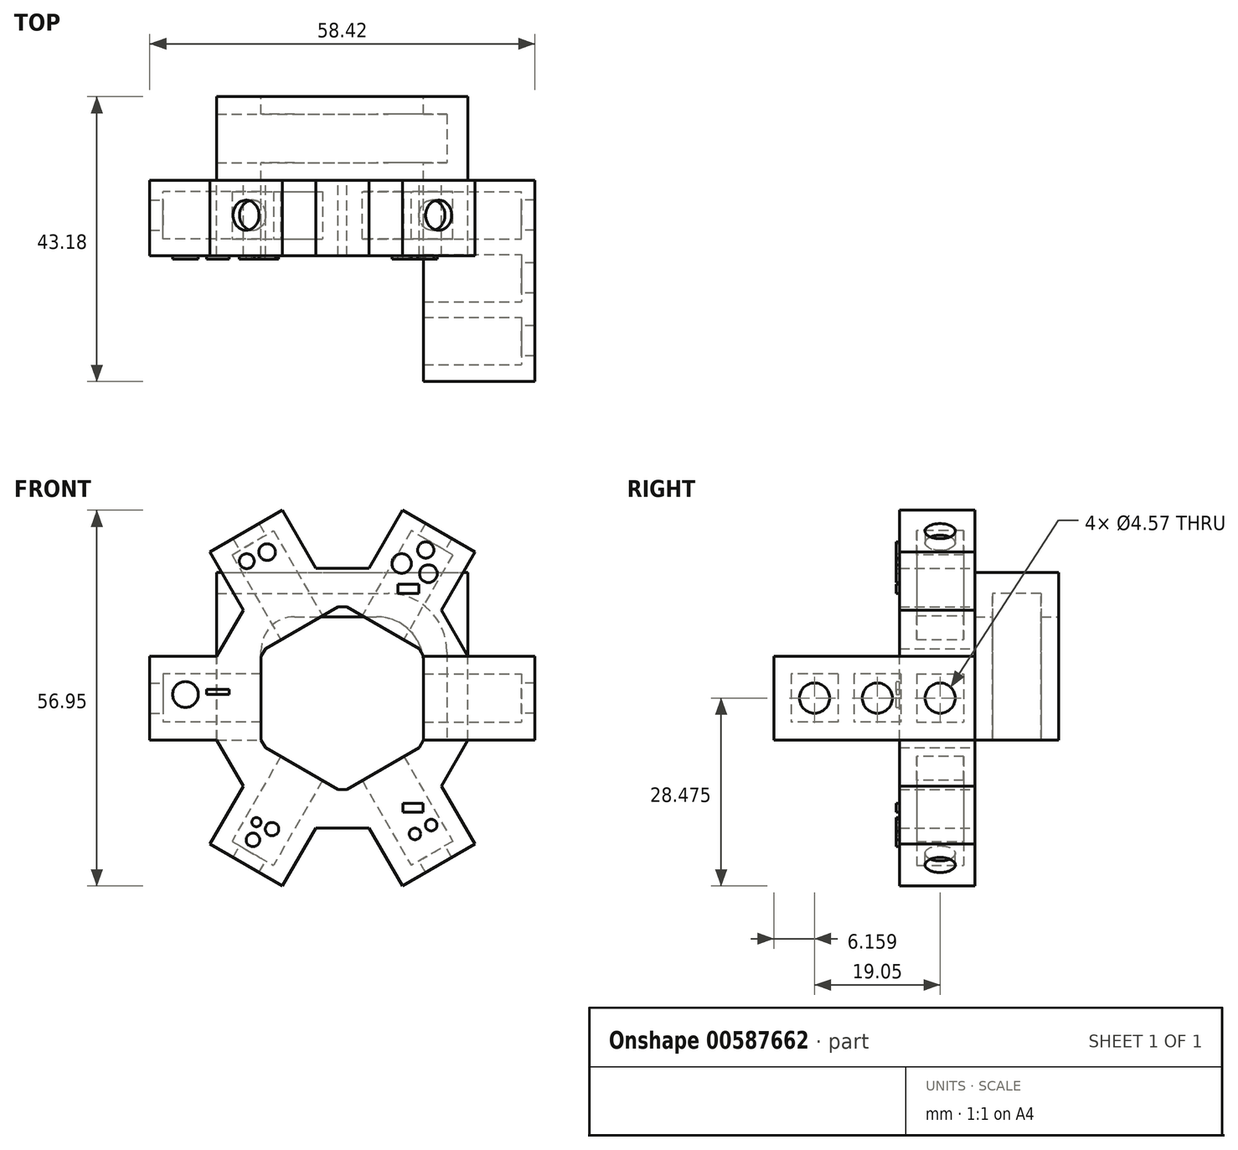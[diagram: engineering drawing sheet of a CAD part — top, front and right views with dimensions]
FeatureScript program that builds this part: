
annotation { "Feature Type Name" : "Feature", "Feature Type Description" : "" }
export const myFeature = defineFeature(function(context is Context, id is Id, definition is map)
    precondition{}
    {
        {
            var Q0;
            Q0=qCreatedBy(makeId("Front.planeOp"),FACE);
            var sketch = newSketch(context, id + "F0", { "sketchPlane" : qUnion([Q0])});
            skLineSegment(sketch, "E0", {"start": v(0, 0) * mm, "end": v(13.34, 0) * mm});
            skLineSegment(sketch, "E1", {"start": v(22.23, -8.89) * mm, "end": v(22.23, -22.23) * mm});
            skPoint(sketch, "E2.visualSharp", {"position": v(22.23, 0) * mm});
            skArc(sketch, "E2.filletArc", {"start": v(22.23, -8.89) * mm, "mid": v(19.62, -2.6) * mm, "end": v(13.34, 0) * mm});
            skLineSegment(sketch, "E3", {"start": v(0, 0) * mm, "end": v(0, 3.18) * mm});
            skLineSegment(sketch, "E4", {"start": v(0, 3.18) * mm, "end": v(25.4, 3.18) * mm});
            skLineSegment(sketch, "E5", {"start": v(25.4, 3.18) * mm, "end": v(25.4, -22.23) * mm});
            skLineSegment(sketch, "E6", {"start": v(25.4, -22.23) * mm, "end": v(22.23, -22.23) * mm});
            skLineSegment(sketch, "E7", {"start": v(0, -3.56) * mm, "end": v(0, 0) * mm});
            skLineSegment(sketch, "E8", {"start": v(18.67, -22.23) * mm, "end": v(22.23, -22.23) * mm});
            skLineSegment(sketch, "E9", {"start": v(0, -3.56) * mm, "end": v(11.56, -3.56) * mm});
            skLineSegment(sketch, "E10", {"start": v(18.67, -10.67) * mm, "end": v(18.67, -22.23) * mm});
            skPoint(sketch, "E11.visualSharp", {"position": v(18.67, -3.56) * mm});
            skArc(sketch, "E11.filletArc", {"start": v(18.67, -10.67) * mm, "mid": v(16.59, -5.64) * mm, "end": v(11.56, -3.56) * mm});
            skLineSegment(sketch, "E12", {"start": v(0, 3.18) * mm, "end": v(-12.7, 3.18) * mm});
            skLineSegment(sketch, "E13", {"start": v(-12.7, 3.17) * mm, "end": v(-12.7, -22.23) * mm});
            skLineSegment(sketch, "E14", {"start": v(0, 0) * mm, "end": v(-12.7, 0) * mm});
            skLineSegment(sketch, "E15", {"start": v(0, -3.56) * mm, "end": v(-0.89, -3.56) * mm});
            skLineSegment(sketch, "E16", {"start": v(-12.7, -22.23) * mm, "end": v(-5.97, -22.23) * mm});
            skLineSegment(sketch, "E17", {"start": v(-5.97, -22.23) * mm, "end": v(-5.97, -8.64) * mm});
            skArc(sketch, "E18.filletArc", {"start": v(-0.89, -3.56) * mm, "mid": v(-4.48, -5.04) * mm, "end": v(-5.97, -8.64) * mm});
            skSolve(sketch);
        }
        {
            var Q0;
            Q0=makeQuery(id+"F0.imprint","IMPRINT",FACE,{"disambiguationData":[TD([[makeQuery(id+"F0.imprint","IMPRINT",EDGE,{"derivedFrom":sQuery(id+"F0.wireOp",EDGE,"E0")}),1.0]])]});
            var Q1;
            Q1=makeQuery(id+"F0.imprint","IMPRINT",FACE,{"disambiguationData":[TD([[makeQuery(id+"F0.imprint","IMPRINT",EDGE,{"derivedFrom":sQuery(id+"F0.wireOp",EDGE,"E0")}),-1.0]])]});
            var Q2;
            Q2=makeQuery(id+"F0.imprint","IMPRINT",FACE,{"disambiguationData":[TD([[makeQuery(id+"F0.imprint","IMPRINT",EDGE,{"derivedFrom":sQuery(id+"F0.wireOp",EDGE,"E3")}),1.0]])]});
            var Q3;
            {var subQ4=sQuery(id+"F0.wireOp",EDGE,"E7");Q3=makeQuery(id+"F0.imprint","IMPRINT",FACE,{"disambiguationData":[TD([[makeQuery(id+"F0.imprint","IMPRINT",EDGE,{"derivedFrom":subQ4}),1.0]])]});}
            var Q4;
            {var subQ0=sQuery(id+"F0.wireOp",EDGE,"E16");Q4=makeQuery(id+"F0.imprint","IMPRINT",FACE,{"disambiguationData":[TD([[makeQuery(id+"F0.imprint","IMPRINT",EDGE,{"derivedFrom":subQ0}),1.0]])]});}
            extrude(context, id + "F1", {"entities" : qUnion([Q0, Q1, Q2, Q3, Q4]), "endBound" : BoundingType.SYMMETRIC, "depth" : 12.7 * mm, "offsetDistance" : 25.4 * mm});
        }
        {
            var Q0;
            Q0=makeQuery(id+"F0.imprint","IMPRINT",FACE,{"disambiguationData":[TD([[makeQuery(id+"F0.imprint","IMPRINT",EDGE,{"derivedFrom":sQuery(id+"F0.wireOp",EDGE,"E0")}),-1.0]])]});
            var Q1;
            {var subQ0=sQuery(id+"F0.wireOp",EDGE,"E16");Q1=makeQuery(id+"F0.imprint","IMPRINT",FACE,{"disambiguationData":[TD([[makeQuery(id+"F0.imprint","IMPRINT",EDGE,{"derivedFrom":subQ0}),1.0]])]});}
            var Q2;
            {var subQ4=sQuery(id+"F0.wireOp",EDGE,"E7");Q2=makeQuery(id+"F0.imprint","IMPRINT",FACE,{"disambiguationData":[TD([[makeQuery(id+"F0.imprint","IMPRINT",EDGE,{"derivedFrom":subQ4}),1.0]])]});}
            extrude(context, id + "F2", {"entities" : qUnion([Q0, Q1, Q2]), "operationType" : NewBodyOperationType.REMOVE, "endBound" : BoundingType.SYMMETRIC, "oppositeDirection" : true, "depth" : 7.37 * mm, "offsetDistance" : 25.4 * mm});
        }
        {
            var Q0;
            Q0=makeQuery(id+"F1.opExtrude","CAP_FACE",FACE,{"disambiguationData":[OSD([sQuery(id+"F0.wireOp",EDGE,"E4"),sQuery(id+"F0.wireOp",EDGE,"E5"),sQuery(id+"F0.wireOp",EDGE,"E6"),sQuery(id+"F0.wireOp",EDGE,"E8"),sQuery(id+"F0.wireOp",EDGE,"E9"),sQuery(id+"F0.wireOp",EDGE,"E10"),sQuery(id+"F0.wireOp",EDGE,"E11.filletArc"),sQuery(id+"F0.wireOp",EDGE,"E12"),sQuery(id+"F0.wireOp",EDGE,"E13"),sQuery(id+"F0.wireOp",EDGE,"E15"),sQuery(id+"F0.wireOp",EDGE,"E16"),sQuery(id+"F0.wireOp",EDGE,"E17"),sQuery(id+"F0.wireOp",EDGE,"E18.filletArc")])],"isStart":false});
            var sketch = newSketch(context, id + "F3", { "sketchPlane" : qUnion([Q0])});
            skLineSegment(sketch, "E19.bottom", {"start": v(18.67, -22.23) * mm, "end": v(25.4, -22.23) * mm});
            skLineSegment(sketch, "E19.top", {"start": v(18.67, -9.52) * mm, "end": v(25.4, -9.52) * mm});
            skLineSegment(sketch, "E19.left", {"start": v(18.67, -22.23) * mm, "end": v(18.67, -9.52) * mm});
            skLineSegment(sketch, "E19.right", {"start": v(25.4, -22.23) * mm, "end": v(25.4, -9.52) * mm});
            skLineSegment(sketch, "E20.bottom", {"start": v(-5.97, -22.23) * mm, "end": v(-12.7, -22.23) * mm});
            skLineSegment(sketch, "E20.top", {"start": v(-5.97, -9.52) * mm, "end": v(-12.7, -9.52) * mm});
            skLineSegment(sketch, "E20.left", {"start": v(-5.97, -22.23) * mm, "end": v(-5.97, -9.52) * mm});
            skLineSegment(sketch, "E20.right", {"start": v(-12.7, -22.23) * mm, "end": v(-12.7, -9.52) * mm});
            skLineSegment(sketch, "E21", {"start": v(18.67, -15.88) * mm, "end": v(25.4, -15.88) * mm, "construction": true});
            skLineSegment(sketch, "E22", {"start": v(-5.97, -15.88) * mm, "end": v(-12.7, -15.88) * mm, "construction": true});
            skLineSegment(sketch, "E23.0", {"start": v(-12.7, 0) * mm, "end": v(13.34, 0) * mm, "construction": true});
            skSolve(sketch);
        }
        {
            var Q0;
            {var subQ3=sQuery(id+"F3.wireOp",EDGE,"E19.bottom");Q0=makeQuery(id+"F3.imprint","IMPRINT",FACE,{"disambiguationData":[TD([[makeQuery(id+"F3.imprint","IMPRINT",EDGE,{"derivedFrom":subQ3}),-1.0]])]});}
            extrude(context, id + "F4", {"entities" : qUnion([Q0]), "operationType" : NewBodyOperationType.ADD, "depth" : 30.48 * mm, "offsetDistance" : 25.4 * mm});
        }
        {
            var Q0;
            Q0=makeQuery(id+"F4.boolean.opBoolean","MERGE",FACE,{"derivedFrom":[makeQuery(id+"F1.opExtrude","SWEPT_FACE",FACE,{"disambiguationData":[OSD([sQuery(id+"F0.wireOp",EDGE,"E5")])]}),makeQuery(id+"F4.opExtrude","SWEPT_FACE",FACE,{"disambiguationData":[OSD([sQuery(id+"F3.wireOp",EDGE,"E19.right")])]})]});
            var sketch = newSketch(context, id + "F5", { "sketchPlane" : qUnion([Q0])});
            skLineSegment(sketch, "E24.bottom", {"start": v(-15.2, -12.23) * mm, "end": v(-8.04, -12.23) * mm});
            skLineSegment(sketch, "E24.top", {"start": v(-15.2, -19.52) * mm, "end": v(-8.04, -19.52) * mm});
            skLineSegment(sketch, "E24.left", {"start": v(-15.2, -12.23) * mm, "end": v(-15.2, -19.52) * mm});
            skLineSegment(sketch, "E24.right", {"start": v(-8.04, -12.23) * mm, "end": v(-8.04, -19.52) * mm});
            skLineSegment(sketch, "E25", {"start": v(-15.2, -15.88) * mm, "end": v(-8.04, -15.88) * mm, "construction": true});
            skLineSegment(sketch, "E26.0", {"start": v(3.68, 0) * mm, "end": v(-3.68, 0) * mm, "construction": true});
            skLineSegment(sketch, "E27", {"start": v(-11.62, -15.88) * mm, "end": v(-11.62, -12.23) * mm, "construction": true});
            skLineSegment(sketch, "E28.bottom", {"start": v(-17.56, -12.23) * mm, "end": v(-24.73, -12.23) * mm});
            skLineSegment(sketch, "E28.top", {"start": v(-17.56, -19.52) * mm, "end": v(-24.73, -19.52) * mm});
            skLineSegment(sketch, "E28.left", {"start": v(-17.56, -12.23) * mm, "end": v(-17.56, -19.52) * mm});
            skLineSegment(sketch, "E28.right", {"start": v(-24.73, -12.23) * mm, "end": v(-24.73, -19.52) * mm});
            skLineSegment(sketch, "E29.bottom", {"start": v(-27.09, -12.23) * mm, "end": v(-34.25, -12.23) * mm});
            skLineSegment(sketch, "E29.top", {"start": v(-27.09, -19.52) * mm, "end": v(-34.25, -19.52) * mm});
            skLineSegment(sketch, "E29.left", {"start": v(-27.09, -12.23) * mm, "end": v(-27.09, -19.52) * mm});
            skLineSegment(sketch, "E29.right", {"start": v(-34.25, -12.23) * mm, "end": v(-34.25, -19.52) * mm});
            skLineSegment(sketch, "E30", {"start": v(-21.15, -19.52) * mm, "end": v(-21.15, -12.23) * mm, "construction": true});
            skLineSegment(sketch, "E31", {"start": v(-30.67, -19.52) * mm, "end": v(-30.67, -12.23) * mm, "construction": true});
            skSolve(sketch);
        }
        {
            var Q0;
            Q0=qSketchRegion(id+"F5",true);
            extrude(context, id + "F6", {"entities" : qUnion([Q0]), "operationType" : NewBodyOperationType.REMOVE, "endBound" : BoundingType.THROUGH_ALL, "oppositeDirection" : true, "depth" : 25.4 * mm, "offsetDistance" : 25.4 * mm});
        }
        {
            var Q0;
            Q0=makeQuery(id+"F3.imprint","IMPRINT",FACE,{"disambiguationData":[TD([[makeQuery(id+"F3.imprint","IMPRINT",EDGE,{"derivedFrom":sQuery(id+"F3.wireOp",EDGE,"E20.bottom")}),1.0]])]});
            extrude(context, id + "F7", {"entities" : qUnion([Q0]), "operationType" : NewBodyOperationType.ADD, "depth" : 11.43 * mm, "offsetDistance" : 25.4 * mm});
        }
        {
            var Q0;
            Q0=makeQuery(id+"F7.boolean.opBoolean","MERGE",FACE,{"derivedFrom":[makeQuery(id+"F1.opExtrude","SWEPT_FACE",FACE,{"disambiguationData":[OSD([sQuery(id+"F0.wireOp",EDGE,"E13")])]}),makeQuery(id+"F7.opExtrude","SWEPT_FACE",FACE,{"disambiguationData":[OSD([sQuery(id+"F3.wireOp",EDGE,"E20.right")])]})]});
            var sketch = newSketch(context, id + "F8", { "sketchPlane" : qUnion([Q0])});
            skLineSegment(sketch, "E32.0", {"start": v(15.2, -12.23) * mm, "end": v(8.04, -12.23) * mm});
            skLineSegment(sketch, "E32.1", {"start": v(15.2, -19.52) * mm, "end": v(8.04, -19.52) * mm});
            skLineSegment(sketch, "E32.2", {"start": v(15.2, -12.23) * mm, "end": v(15.2, -19.52) * mm});
            skLineSegment(sketch, "E32.3", {"start": v(8.04, -12.23) * mm, "end": v(8.04, -19.52) * mm});
            skLineSegment(sketch, "E32.4", {"start": v(15.2, -15.88) * mm, "end": v(8.04, -15.88) * mm});
            skLineSegment(sketch, "E32.5", {"start": v(-3.68, 0) * mm, "end": v(3.68, 0) * mm});
            skLineSegment(sketch, "E32.6", {"start": v(11.62, -15.88) * mm, "end": v(11.62, -12.23) * mm});
            skSolve(sketch);
        }
        {
            var Q0;
            Q0 = qSketchRegion(id + "F8", true);
            extrude(context, id + "F9", {"entities" : qUnion([Q0]), "operationType" : NewBodyOperationType.REMOVE, "oppositeDirection" : true, "depth" : 12.7 * mm, "offsetDistance" : 25.4 * mm});
        }
        {
            var Q0;
            {var subQ3=sQuery(id+"F3.wireOp",EDGE,"E19.top");Q0=makeQuery(id+"F3.imprint","IMPRINT",FACE,{"disambiguationData":[TD([[makeQuery(id+"F3.imprint","IMPRINT",EDGE,{"derivedFrom":subQ3}),1.0]])]});}
            var sketch = newSketch(context, id + "F10", { "sketchPlane" : qUnion([Q0])});
            skLineSegment(sketch, "E33.0", {"start": v(18.67, -12.23) * mm, "end": v(18.67, -19.52) * mm, "construction": true});
            skLineSegment(sketch, "E33.1", {"start": v(-5.97, -12.23) * mm, "end": v(-5.97, -19.52) * mm, "construction": true});
            skCircle(sketch, "E34", {"center": v(6.35, -15.88) * mm, "radius": 6.35 * mm, "construction": true});
            skLineSegment(sketch, "E35", {"start": v(6.35, -15.88) * mm, "end": v(-5.97, -15.88) * mm, "construction": true});
            skLineSegment(sketch, "E36", {"start": v(6.35, -15.88) * mm, "end": v(18.67, -15.88) * mm, "construction": true});
            skLineSegment(sketch, "E37", {"start": v(6.35, -15.88) * mm, "end": v(0.2, -5.2) * mm, "construction": true});
            skLineSegment(sketch, "E38", {"start": v(6.35, -15.88) * mm, "end": v(12.5, -5.2) * mm, "construction": true});
            skLineSegment(sketch, "E39", {"start": v(6.35, -15.87) * mm, "end": v(0.2, -26.54) * mm, "construction": true});
            skLineSegment(sketch, "E40", {"start": v(6.35, -15.88) * mm, "end": v(12.5, -26.54) * mm, "construction": true});
            skLineSegment(sketch, "E41", {"start": v(-5.3, -8.38) * mm, "end": v(5.69, -2.03) * mm});
            skLineSegment(sketch, "E42", {"start": v(5.69, -2.03) * mm, "end": v(2.32, 3.8) * mm, "construction": true});
            skLineSegment(sketch, "E43", {"start": v(2.32, 3.8) * mm, "end": v(-8.67, -2.55) * mm});
            skLineSegment(sketch, "E44", {"start": v(-8.67, -2.55) * mm, "end": v(-5.3, -8.38) * mm, "construction": true});
            skLineSegment(sketch, "E45.0", {"start": v(-5.97, -9.52) * mm, "end": v(-12.7, -9.52) * mm});
            skLineSegment(sketch, "E46.1", {"start": v(-12.7, -22.23) * mm, "end": v(-12.7, -9.52) * mm, "construction": true});
            skLineSegment(sketch, "E47", {"start": v(7.01, -2.03) * mm, "end": v(18, -8.38) * mm});
            skLineSegment(sketch, "E48", {"start": v(18, -8.38) * mm, "end": v(21.37, -2.55) * mm, "construction": true});
            skLineSegment(sketch, "E49", {"start": v(21.37, -2.55) * mm, "end": v(10.38, 3.8) * mm});
            skLineSegment(sketch, "E50", {"start": v(10.38, 3.8) * mm, "end": v(7.01, -2.03) * mm, "construction": true});
            skLineSegment(sketch, "E51", {"start": v(7.01, -29.72) * mm, "end": v(18, -23.37) * mm});
            skLineSegment(sketch, "E52", {"start": v(18, -23.37) * mm, "end": v(21.37, -29.2) * mm, "construction": true});
            skLineSegment(sketch, "E53", {"start": v(7.01, -29.72) * mm, "end": v(10.38, -35.55) * mm, "construction": true});
            skLineSegment(sketch, "E54", {"start": v(10.38, -35.55) * mm, "end": v(21.37, -29.2) * mm});
            skLineSegment(sketch, "E55", {"start": v(-5.3, -23.37) * mm, "end": v(5.69, -29.72) * mm});
            skLineSegment(sketch, "E56", {"start": v(5.69, -29.72) * mm, "end": v(2.32, -35.55) * mm, "construction": true});
            skLineSegment(sketch, "E57", {"start": v(-5.3, -23.37) * mm, "end": v(-8.67, -29.2) * mm, "construction": true});
            skLineSegment(sketch, "E58", {"start": v(-8.67, -29.2) * mm, "end": v(2.32, -35.55) * mm});
            skLineSegment(sketch, "E59", {"start": v(-5.3, -8.38) * mm, "end": v(-5.97, -9.52) * mm});
            skLineSegment(sketch, "E60", {"start": v(-8.67, -2.55) * mm, "end": v(-12.7, -9.52) * mm});
            skLineSegment(sketch, "E61", {"start": v(5.69, -2.03) * mm, "end": v(7.01, -2.03) * mm});
            skLineSegment(sketch, "E62", {"start": v(2.32, 3.8) * mm, "end": v(10.38, 3.8) * mm});
            skLineSegment(sketch, "E63", {"start": v(18, -8.38) * mm, "end": v(18.67, -9.52) * mm});
            skLineSegment(sketch, "E64.0", {"start": v(18.67, -9.52) * mm, "end": v(25.4, -9.52) * mm});
            skLineSegment(sketch, "E65", {"start": v(21.37, -2.55) * mm, "end": v(25.4, -9.52) * mm});
            skLineSegment(sketch, "E66.0", {"start": v(-5.97, -22.23) * mm, "end": v(-12.7, -22.23) * mm});
            skLineSegment(sketch, "E66.1", {"start": v(18.67, -22.23) * mm, "end": v(25.4, -22.23) * mm});
            skLineSegment(sketch, "E67", {"start": v(18.67, -22.23) * mm, "end": v(18, -23.37) * mm});
            skLineSegment(sketch, "E68", {"start": v(21.37, -29.2) * mm, "end": v(25.4, -22.23) * mm});
            skLineSegment(sketch, "E69", {"start": v(7.01, -29.72) * mm, "end": v(5.69, -29.72) * mm});
            skLineSegment(sketch, "E70", {"start": v(2.32, -35.55) * mm, "end": v(10.38, -35.55) * mm});
            skLineSegment(sketch, "E71", {"start": v(-5.3, -23.37) * mm, "end": v(-5.97, -22.23) * mm});
            skLineSegment(sketch, "E72", {"start": v(-8.67, -29.2) * mm, "end": v(-12.7, -22.23) * mm});
            skSolve(sketch);
        }
        {
            var Q0;
            Q0 = qSketchRegion(id + "F10", true);
            var Q1;
            Q1=makeQuery(id+"F7.opExtrude","CAP_FACE",FACE,{"disambiguationData":[OSD([sQuery(id+"F3.wireOp",EDGE,"E20.bottom"),sQuery(id+"F3.wireOp",EDGE,"E20.top"),sQuery(id+"F3.wireOp",EDGE,"E20.left"),sQuery(id+"F3.wireOp",EDGE,"E20.right")])],"isStart":false});
            extrude(context, id + "F11", {"entities" : qUnion([Q0]), "operationType" : NewBodyOperationType.ADD, "endBound" : BoundingType.UP_TO_SURFACE, "depth" : 25.4 * mm, "endBoundEntityFace" : qUnion([Q1]), "offsetDistance" : 25.4 * mm});
        }
        {
            var Q0;
            Q0=makeQuery(id+"F11.opExtrude","SWEPT_FACE",FACE,{"disambiguationData":[OSD([sQuery(id+"F10.wireOp",EDGE,"E41")])]});
            var sketch = newSketch(context, id + "F12", { "sketchPlane" : qUnion([Q0])});
            skLineSegment(sketch, "E73.bottom", {"start": v(1.2, 15.2) * mm, "end": v(-6.08, 15.2) * mm});
            skLineSegment(sketch, "E73.top", {"start": v(1.2, 8.04) * mm, "end": v(-6.08, 8.04) * mm});
            skLineSegment(sketch, "E73.left", {"start": v(1.2, 15.2) * mm, "end": v(1.2, 8.04) * mm});
            skLineSegment(sketch, "E73.right", {"start": v(-6.08, 15.2) * mm, "end": v(-6.08, 8.04) * mm});
            skLineSegment(sketch, "E74.0", {"start": v(-11.28, 15.2) * mm, "end": v(-11.28, 8.04) * mm, "construction": true});
            skLineSegment(sketch, "E75", {"start": v(-11.28, 15.2) * mm, "end": v(-6.08, 15.2) * mm, "construction": true});
            skLineSegment(sketch, "E76", {"start": v(-11.28, 8.04) * mm, "end": v(-6.08, 8.04) * mm, "construction": true});
            skLineSegment(sketch, "E77", {"start": v(-2.44, 15.2) * mm, "end": v(-2.44, 17.78) * mm, "construction": true});
            skSolve(sketch);
        }
        {
            var Q0;
            Q0 = qSketchRegion(id + "F12", true);
            var Q1;
            Q1=makeQuery(id+"F11.opExtrude","SWEPT_FACE",FACE,{"disambiguationData":[OSD([sQuery(id+"F10.wireOp",EDGE,"E43")])]});
            var Q2;
            Q2=makeQuery(id+"F11.opExtrude","SWEPT_FACE",FACE,{"disambiguationData":[OSD([sQuery(id+"F10.wireOp",EDGE,"E54")])]});
            extrude(context, id + "F13", {"entities" : qUnion([Q0]), "operationType" : NewBodyOperationType.REMOVE, "endBound" : BoundingType.UP_TO_SURFACE, "oppositeDirection" : true, "depth" : 25.4 * mm, "endBoundEntityFace" : qUnion([Q1]), "offsetDistance" : 25.4 * mm, "hasSecondDirection" : true, "secondDirectionBound" : SecondDirectionBoundingType.UP_TO_SURFACE, "secondDirectionOppositeDirection" : false, "secondDirectionDepth" : 25.4 * mm, "secondDirectionBoundEntityFace" : qUnion([Q2])});
        }
        {
            var Q0;
            Q0=makeQuery(id+"F11.opExtrude","SWEPT_FACE",FACE,{"disambiguationData":[OSD([sQuery(id+"F10.wireOp",EDGE,"E47")])]});
            var sketch = newSketch(context, id + "F14", { "sketchPlane" : qUnion([Q0])});
            skLineSegment(sketch, "E78.bottom", {"start": v(9.8, 8.04) * mm, "end": v(17.08, 8.04) * mm});
            skLineSegment(sketch, "E78.top", {"start": v(9.8, 15.2) * mm, "end": v(17.08, 15.2) * mm});
            skLineSegment(sketch, "E78.left", {"start": v(9.8, 8.04) * mm, "end": v(9.8, 15.2) * mm});
            skLineSegment(sketch, "E78.right", {"start": v(17.08, 8.04) * mm, "end": v(17.08, 15.2) * mm});
            skLineSegment(sketch, "E79.0", {"start": v(22.28, 15.2) * mm, "end": v(22.28, 8.04) * mm, "construction": true});
            skLineSegment(sketch, "E80", {"start": v(22.28, 15.2) * mm, "end": v(17.08, 15.2) * mm, "construction": true});
            skLineSegment(sketch, "E81", {"start": v(22.28, 8.04) * mm, "end": v(17.08, 8.04) * mm, "construction": true});
            skLineSegment(sketch, "E82", {"start": v(13.44, 17.78) * mm, "end": v(13.44, 15.2) * mm, "construction": true});
            skPoint(sketch, "E82.endSnap0", {"position": v(13.44, 15.2) * mm});
            skSolve(sketch);
        }
        {
            var Q0;
            Q0 = qSketchRegion(id + "F14", true);
            var Q1;
            Q1=makeQuery(id+"F11.opExtrude","SWEPT_FACE",FACE,{"disambiguationData":[OSD([sQuery(id+"F10.wireOp",EDGE,"E49")])]});
            var Q2;
            Q2=makeQuery(id+"F11.opExtrude","SWEPT_FACE",FACE,{"disambiguationData":[OSD([sQuery(id+"F10.wireOp",EDGE,"E58")])]});
            extrude(context, id + "F15", {"entities" : qUnion([Q0]), "operationType" : NewBodyOperationType.REMOVE, "endBound" : BoundingType.UP_TO_SURFACE, "oppositeDirection" : true, "depth" : 25.4 * mm, "endBoundEntityFace" : qUnion([Q1]), "offsetDistance" : 25.4 * mm, "hasSecondDirection" : true, "secondDirectionBound" : SecondDirectionBoundingType.UP_TO_SURFACE, "secondDirectionOppositeDirection" : false, "secondDirectionDepth" : 25.4 * mm, "secondDirectionBoundEntityFace" : qUnion([Q2])});
        }
        {
            var Q0;
            Q0=makeQuery(id+"F4.boolean.opBoolean","MERGE",FACE,{"derivedFrom":[makeQuery(id+"F1.opExtrude","SWEPT_FACE",FACE,{"disambiguationData":[OSD([sQuery(id+"F0.wireOp",EDGE,"E5")])]}),makeQuery(id+"F4.opExtrude","SWEPT_FACE",FACE,{"disambiguationData":[OSD([sQuery(id+"F3.wireOp",EDGE,"E19.right")])]})]});
            var sketch = newSketch(context, id + "F16", { "sketchPlane" : qUnion([Q0])});
            skLineSegment(sketch, "E83.0", {"start": v(-36.83, -9.53) * mm, "end": v(-17.78, -9.53) * mm});
            skLineSegment(sketch, "E83.1", {"start": v(-17.78, -9.53) * mm, "end": v(-6.35, -9.53) * mm});
            skLineSegment(sketch, "E83.2", {"start": v(-6.35, -22.23) * mm, "end": v(-6.35, -9.53) * mm});
            skLineSegment(sketch, "E83.3", {"start": v(-17.78, -22.23) * mm, "end": v(-6.35, -22.23) * mm});
            skLineSegment(sketch, "E83.4", {"start": v(-36.83, -22.23) * mm, "end": v(-17.78, -22.23) * mm});
            skLineSegment(sketch, "E83.5", {"start": v(-36.83, -9.53) * mm, "end": v(-36.83, -22.23) * mm});
            skLineSegment(sketch, "E84.0", {"start": v(-27.09, -12.23) * mm, "end": v(-34.25, -12.23) * mm});
            skLineSegment(sketch, "E84.1", {"start": v(-27.09, -12.23) * mm, "end": v(-27.09, -19.52) * mm});
            skLineSegment(sketch, "E84.2", {"start": v(-34.25, -12.23) * mm, "end": v(-34.25, -19.52) * mm});
            skLineSegment(sketch, "E84.3", {"start": v(-27.09, -19.52) * mm, "end": v(-34.25, -19.52) * mm});
            skLineSegment(sketch, "E84.4", {"start": v(-17.56, -19.52) * mm, "end": v(-24.73, -19.52) * mm});
            skLineSegment(sketch, "E84.5", {"start": v(-24.73, -12.23) * mm, "end": v(-24.73, -19.52) * mm});
            skLineSegment(sketch, "E84.6", {"start": v(-17.56, -12.23) * mm, "end": v(-24.73, -12.23) * mm});
            skLineSegment(sketch, "E84.7", {"start": v(-17.56, -12.23) * mm, "end": v(-17.56, -19.52) * mm});
            skLineSegment(sketch, "E84.8", {"start": v(-15.2, -12.23) * mm, "end": v(-15.2, -19.52) * mm});
            skLineSegment(sketch, "E84.9", {"start": v(-15.2, -12.23) * mm, "end": v(-8.04, -12.23) * mm});
            skLineSegment(sketch, "E84.10", {"start": v(-8.04, -12.23) * mm, "end": v(-8.04, -19.52) * mm});
            skLineSegment(sketch, "E84.11", {"start": v(-15.2, -19.52) * mm, "end": v(-8.04, -19.52) * mm});
            skSolve(sketch);
        }
        {
            var Q0;
            Q0 = qSketchRegion(id + "F16", true);
            extrude(context, id + "F17", {"entities" : qUnion([Q0]), "operationType" : NewBodyOperationType.ADD, "depth" : 8.13 * mm, "offsetDistance" : 25.4 * mm});
        }
        {
            var Q0;
            Q0=makeQuery(id+"F11.opExtrude","SWEPT_FACE",FACE,{"disambiguationData":[OSD([sQuery(id+"F10.wireOp",EDGE,"E49")])]});
            extrude(context, id + "F18", {"entities" : qUnion([Q0]), "operationType" : NewBodyOperationType.ADD, "depth" : 8.13 * mm, "offsetDistance" : 25.4 * mm});
        }
        {
            var Q0;
            Q0=makeQuery(id+"F11.opExtrude","SWEPT_FACE",FACE,{"disambiguationData":[OSD([sQuery(id+"F10.wireOp",EDGE,"E43")])]});
            extrude(context, id + "F19", {"entities" : qUnion([Q0]), "operationType" : NewBodyOperationType.ADD, "depth" : 8.13 * mm, "offsetDistance" : 25.4 * mm});
        }
        {
            var Q0;
            Q0=makeQuery(id+"F7.boolean.opBoolean","MERGE",FACE,{"derivedFrom":[makeQuery(id+"F1.opExtrude","SWEPT_FACE",FACE,{"disambiguationData":[OSD([sQuery(id+"F0.wireOp",EDGE,"E13")])]}),makeQuery(id+"F7.opExtrude","SWEPT_FACE",FACE,{"disambiguationData":[OSD([sQuery(id+"F3.wireOp",EDGE,"E20.right")])]})]});
            var sketch = newSketch(context, id + "F20", { "sketchPlane" : qUnion([Q0])});
            skLineSegment(sketch, "E85.0", {"start": v(17.78, -9.52) * mm, "end": v(6.35, -9.52) * mm});
            skLineSegment(sketch, "E85.1", {"start": v(6.35, -22.23) * mm, "end": v(6.35, -9.52) * mm});
            skLineSegment(sketch, "E85.2", {"start": v(17.78, -22.23) * mm, "end": v(6.35, -22.23) * mm});
            skLineSegment(sketch, "E85.3", {"start": v(17.78, -9.52) * mm, "end": v(17.78, -22.23) * mm});
            skLineSegment(sketch, "E85.4", {"start": v(15.2, -12.23) * mm, "end": v(8.04, -12.23) * mm});
            skLineSegment(sketch, "E85.5", {"start": v(8.04, -12.23) * mm, "end": v(8.04, -19.52) * mm});
            skLineSegment(sketch, "E85.6", {"start": v(15.2, -19.52) * mm, "end": v(8.04, -19.52) * mm});
            skLineSegment(sketch, "E85.7", {"start": v(15.2, -12.23) * mm, "end": v(15.2, -19.52) * mm});
            skSolve(sketch);
        }
        {
            var Q0;
            Q0 = qSketchRegion(id + "F20", true);
            extrude(context, id + "F21", {"entities" : qUnion([Q0]), "operationType" : NewBodyOperationType.ADD, "depth" : 8.13 * mm, "offsetDistance" : 25.4 * mm});
        }
        {
            var Q0;
            Q0=makeQuery(id+"F11.opExtrude","SWEPT_FACE",FACE,{"disambiguationData":[OSD([sQuery(id+"F10.wireOp",EDGE,"E58")])]});
            extrude(context, id + "F22", {"entities" : qUnion([Q0]), "operationType" : NewBodyOperationType.ADD, "depth" : 8.13 * mm, "offsetDistance" : 25.4 * mm});
        }
        {
            var Q0;
            Q0=makeQuery(id+"F11.opExtrude","SWEPT_FACE",FACE,{"disambiguationData":[OSD([sQuery(id+"F10.wireOp",EDGE,"E54")])]});
            extrude(context, id + "F23", {"entities" : qUnion([Q0]), "operationType" : NewBodyOperationType.ADD, "depth" : 8.13 * mm, "offsetDistance" : 25.4 * mm});
        }
        {
            var Q0;
            Q0=makeQuery(id+"F18.opExtrude","CAP_FACE",FACE,{"disambiguationData":[OSD([sQuery(id+"F10.wireOp",EDGE,"E49")])],"isStart":false});
            var sketch = newSketch(context, id + "F24", { "sketchPlane" : qUnion([Q0])});
            skLineSegment(sketch, "E86.0", {"start": v(7.09, -17.78) * mm, "end": v(7.09, -6.35) * mm});
            skLineSegment(sketch, "E86.1", {"start": v(19.79, -6.35) * mm, "end": v(7.09, -6.35) * mm});
            skLineSegment(sketch, "E86.2", {"start": v(19.79, -17.78) * mm, "end": v(7.09, -17.78) * mm});
            skLineSegment(sketch, "E86.3", {"start": v(19.79, -17.78) * mm, "end": v(19.79, -6.35) * mm});
            skLineSegment(sketch, "E87", {"start": v(9.8, -8.04) * mm, "end": v(17.08, -15.2) * mm, "construction": true});
            skCircle(sketch, "E88", {"center": v(13.44, -11.62) * mm, "radius": 2.29 * mm});
            skSolve(sketch);
        }
        {
            var Q0;
            Q0 = qSketchRegion(id + "F24", true);
            extrude(context, id + "F25", {"entities" : qUnion([Q0]), "operationType" : NewBodyOperationType.ADD, "depth" : 2.03 * mm, "offsetDistance" : 25.4 * mm});
        }
        {
            var Q0;
            Q0=makeQuery(id+"F19.opExtrude","CAP_FACE",FACE,{"disambiguationData":[OSD([sQuery(id+"F10.wireOp",EDGE,"E43")])],"isStart":false});
            var sketch = newSketch(context, id + "F26", { "sketchPlane" : qUnion([Q0])});
            skLineSegment(sketch, "E89.0", {"start": v(3.91, -6.35) * mm, "end": v(-8.79, -6.35) * mm});
            skLineSegment(sketch, "E89.1", {"start": v(3.91, -17.78) * mm, "end": v(3.91, -6.35) * mm});
            skLineSegment(sketch, "E89.2", {"start": v(-8.79, -17.78) * mm, "end": v(-8.79, -6.35) * mm});
            skLineSegment(sketch, "E89.3", {"start": v(3.91, -17.78) * mm, "end": v(-8.79, -17.78) * mm});
            skLineSegment(sketch, "E90", {"start": v(-6.08, -8.04) * mm, "end": v(1.2, -15.2) * mm, "construction": true});
            skCircle(sketch, "E91", {"center": v(-2.44, -11.62) * mm, "radius": 2.29 * mm});
            skSolve(sketch);
        }
        {
            var Q0;
            Q0 = qSketchRegion(id + "F26", true);
            extrude(context, id + "F27", {"entities" : qUnion([Q0]), "operationType" : NewBodyOperationType.ADD, "depth" : 2.03 * mm, "offsetDistance" : 25.4 * mm});
        }
        {
            var Q0;
            Q0=makeQuery(id+"F21.opExtrude","CAP_FACE",FACE,{"disambiguationData":[OSD([sQuery(id+"F20.wireOp",EDGE,"E85.0"),sQuery(id+"F20.wireOp",EDGE,"E85.1"),sQuery(id+"F20.wireOp",EDGE,"E85.2"),sQuery(id+"F20.wireOp",EDGE,"E85.3"),sQuery(id+"F20.wireOp",EDGE,"E85.4"),sQuery(id+"F20.wireOp",EDGE,"E85.5"),sQuery(id+"F20.wireOp",EDGE,"E85.6"),sQuery(id+"F20.wireOp",EDGE,"E85.7")])],"isStart":false});
            var sketch = newSketch(context, id + "F28", { "sketchPlane" : qUnion([Q0])});
            skLineSegment(sketch, "E92.0", {"start": v(17.78, -9.52) * mm, "end": v(6.35, -9.52) * mm});
            skLineSegment(sketch, "E92.1", {"start": v(6.35, -22.22) * mm, "end": v(6.35, -9.52) * mm});
            skLineSegment(sketch, "E92.2", {"start": v(17.78, -22.22) * mm, "end": v(6.35, -22.22) * mm});
            skLineSegment(sketch, "E92.3", {"start": v(17.78, -9.52) * mm, "end": v(17.78, -22.22) * mm});
            skLineSegment(sketch, "E93", {"start": v(8.04, -12.23) * mm, "end": v(15.2, -19.52) * mm, "construction": true});
            skCircle(sketch, "E94", {"center": v(11.62, -15.88) * mm, "radius": 2.29 * mm});
            skSolve(sketch);
        }
        {
            var Q0;
            Q0 = qSketchRegion(id + "F28", true);
            extrude(context, id + "F29", {"entities" : qUnion([Q0]), "operationType" : NewBodyOperationType.ADD, "depth" : 2.03 * mm, "offsetDistance" : 25.4 * mm});
        }
        {
            var Q0;
            Q0=makeQuery(id+"F22.opExtrude","CAP_FACE",FACE,{"disambiguationData":[OSD([sQuery(id+"F10.wireOp",EDGE,"E58")])],"isStart":false});
            var sketch = newSketch(context, id + "F30", { "sketchPlane" : qUnion([Q0])});
            skLineSegment(sketch, "E95.0", {"start": v(7.09, 17.78) * mm, "end": v(7.09, 6.35) * mm});
            skLineSegment(sketch, "E95.1", {"start": v(7.09, 17.78) * mm, "end": v(19.79, 17.78) * mm});
            skLineSegment(sketch, "E95.2", {"start": v(7.09, 6.35) * mm, "end": v(19.79, 6.35) * mm});
            skLineSegment(sketch, "E95.3", {"start": v(19.79, 17.78) * mm, "end": v(19.79, 6.35) * mm});
            skLineSegment(sketch, "E96", {"start": v(9.8, 15.2) * mm, "end": v(17.08, 8.04) * mm, "construction": true});
            skCircle(sketch, "E97", {"center": v(13.44, 11.62) * mm, "radius": 2.29 * mm});
            skSolve(sketch);
        }
        {
            var Q0;
            Q0 = qSketchRegion(id + "F30", true);
            extrude(context, id + "F31", {"entities" : qUnion([Q0]), "operationType" : NewBodyOperationType.ADD, "depth" : 2.03 * mm, "offsetDistance" : 25.4 * mm});
        }
        {
            var Q0;
            Q0=makeQuery(id+"F23.opExtrude","CAP_FACE",FACE,{"disambiguationData":[OSD([sQuery(id+"F10.wireOp",EDGE,"E54")])],"isStart":false});
            var sketch = newSketch(context, id + "F32", { "sketchPlane" : qUnion([Q0])});
            skLineSegment(sketch, "E98.0", {"start": v(-8.79, 17.78) * mm, "end": v(3.91, 17.78) * mm});
            skLineSegment(sketch, "E98.1", {"start": v(-8.79, 17.78) * mm, "end": v(-8.79, 6.35) * mm});
            skLineSegment(sketch, "E98.2", {"start": v(-8.79, 6.35) * mm, "end": v(3.91, 6.35) * mm});
            skLineSegment(sketch, "E98.3", {"start": v(3.91, 17.78) * mm, "end": v(3.91, 6.35) * mm});
            skLineSegment(sketch, "E99", {"start": v(-6.08, 15.2) * mm, "end": v(1.2, 8.04) * mm, "construction": true});
            skCircle(sketch, "E100", {"center": v(-2.44, 11.62) * mm, "radius": 2.29 * mm});
            skSolve(sketch);
        }
        {
            var Q0;
            Q0 = qSketchRegion(id + "F32", true);
            extrude(context, id + "F33", {"entities" : qUnion([Q0]), "operationType" : NewBodyOperationType.ADD, "depth" : 2.03 * mm, "offsetDistance" : 25.4 * mm});
        }
        {
            var Q0;
            Q0=makeQuery(id+"F17.opExtrude","CAP_FACE",FACE,{"disambiguationData":[OSD([sQuery(id+"F16.wireOp",EDGE,"E83.0"),sQuery(id+"F16.wireOp",EDGE,"E83.1"),sQuery(id+"F16.wireOp",EDGE,"E83.2"),sQuery(id+"F16.wireOp",EDGE,"E83.3"),sQuery(id+"F16.wireOp",EDGE,"E83.4"),sQuery(id+"F16.wireOp",EDGE,"E83.5"),sQuery(id+"F16.wireOp",EDGE,"E84.0"),sQuery(id+"F16.wireOp",EDGE,"E84.1"),sQuery(id+"F16.wireOp",EDGE,"E84.2"),sQuery(id+"F16.wireOp",EDGE,"E84.3"),sQuery(id+"F16.wireOp",EDGE,"E84.4"),sQuery(id+"F16.wireOp",EDGE,"E84.5"),sQuery(id+"F16.wireOp",EDGE,"E84.6"),sQuery(id+"F16.wireOp",EDGE,"E84.7"),sQuery(id+"F16.wireOp",EDGE,"E84.8"),sQuery(id+"F16.wireOp",EDGE,"E84.9"),sQuery(id+"F16.wireOp",EDGE,"E84.10"),sQuery(id+"F16.wireOp",EDGE,"E84.11")])],"isStart":false});
            var sketch = newSketch(context, id + "F34", { "sketchPlane" : qUnion([Q0])});
            skLineSegment(sketch, "E101.0", {"start": v(-36.83, -9.53) * mm, "end": v(-36.83, -22.23) * mm});
            skLineSegment(sketch, "E101.1", {"start": v(-36.83, -22.23) * mm, "end": v(-6.35, -22.23) * mm});
            skLineSegment(sketch, "E101.2", {"start": v(-6.35, -22.23) * mm, "end": v(-6.35, -9.53) * mm});
            skLineSegment(sketch, "E101.3", {"start": v(-36.83, -9.53) * mm, "end": v(-6.35, -9.53) * mm});
            skLineSegment(sketch, "E102", {"start": v(-34.25, -19.52) * mm, "end": v(-27.09, -12.23) * mm, "construction": true});
            skLineSegment(sketch, "E103", {"start": v(-24.73, -19.52) * mm, "end": v(-17.56, -12.23) * mm, "construction": true});
            skLineSegment(sketch, "E104", {"start": v(-15.2, -19.52) * mm, "end": v(-8.04, -12.23) * mm, "construction": true});
            skCircle(sketch, "E105", {"center": v(-30.67, -15.88) * mm, "radius": 2.29 * mm});
            skCircle(sketch, "E106", {"center": v(-21.15, -15.88) * mm, "radius": 2.29 * mm});
            skCircle(sketch, "E107", {"center": v(-11.62, -15.88) * mm, "radius": 2.29 * mm});
            skSolve(sketch);
        }
        {
            var Q0;
            Q0 = qSketchRegion(id + "F34", true);
            extrude(context, id + "F35", {"entities" : qUnion([Q0]), "operationType" : NewBodyOperationType.ADD, "depth" : 2.03 * mm, "offsetDistance" : 25.4 * mm});
        }
        {
            var Q0;
            {var subQ0=sQuery(id+"F3.wireOp",EDGE,"E20.right");var subQ1=sQuery(id+"F3.wireOp",EDGE,"E20.left");var subQ2=sQuery(id+"F3.wireOp",EDGE,"E20.top");var subQ3=sQuery(id+"F3.wireOp",EDGE,"E20.bottom");Q0=makeQuery(id+"F33.boolean.opBoolean","MERGE",FACE,{"derivedFrom":[makeQuery(id+"F31.boolean.opBoolean","MERGE",FACE,{"derivedFrom":[makeQuery(id+"F29.boolean.opBoolean","MERGE",FACE,{"derivedFrom":[makeQuery(id+"F27.boolean.opBoolean","MERGE",FACE,{"derivedFrom":[makeQuery(id+"F25.boolean.opBoolean","MERGE",FACE,{"derivedFrom":[makeQuery(id+"F23.boolean.opBoolean","MERGE",FACE,{"derivedFrom":[makeQuery(id+"F22.boolean.opBoolean","MERGE",FACE,{"derivedFrom":[makeQuery(id+"F21.boolean.opBoolean","MERGE",FACE,{"derivedFrom":[makeQuery(id+"F19.boolean.opBoolean","MERGE",FACE,{"derivedFrom":[makeQuery(id+"F18.boolean.opBoolean","MERGE",FACE,{"derivedFrom":[makeQuery(id+"F11.boolean.opBoolean","MERGE",FACE,{"derivedFrom":[makeQuery(id+"F7.opExtrude","CAP_FACE",FACE,{"disambiguationData":[OSD([subQ3,subQ2,subQ1,subQ0])],"isStart":false}),makeQuery(id+"F11.opExtrude","CAP_FACE",FACE,{"disambiguationData":[OSD([subQ3,subQ2,subQ1,subQ0]),OD(0.0)],"isStart":false}),makeQuery(id+"F11.opExtrude","CAP_FACE",FACE,{"disambiguationData":[OSD([subQ3,subQ2,subQ1,subQ0]),OD(1.0)],"isStart":false})]}),makeQuery(id+"F18.opExtrude","SWEPT_FACE",FACE,{"disambiguationData":[OSD([subQ3,subQ2,subQ1,subQ0,sQuery(id+"F10.wireOp",EDGE,"E49")])]})]}),makeQuery(id+"F19.opExtrude","SWEPT_FACE",FACE,{"disambiguationData":[OSD([subQ3,subQ2,subQ1,subQ0,sQuery(id+"F10.wireOp",EDGE,"E43")])]})]}),makeQuery(id+"F21.opExtrude","SWEPT_FACE",FACE,{"disambiguationData":[OSD([sQuery(id+"F20.wireOp",EDGE,"E85.3")])]})]}),makeQuery(id+"F22.opExtrude","SWEPT_FACE",FACE,{"disambiguationData":[OSD([subQ3,subQ2,subQ1,subQ0,sQuery(id+"F10.wireOp",EDGE,"E58")])]})]}),makeQuery(id+"F23.opExtrude","SWEPT_FACE",FACE,{"disambiguationData":[OSD([subQ3,subQ2,subQ1,subQ0,sQuery(id+"F10.wireOp",EDGE,"E54")])]})]}),makeQuery(id+"F25.opExtrude","SWEPT_FACE",FACE,{"disambiguationData":[OSD([sQuery(id+"F24.wireOp",EDGE,"E86.2")])]})]}),makeQuery(id+"F27.opExtrude","SWEPT_FACE",FACE,{"disambiguationData":[OSD([sQuery(id+"F26.wireOp",EDGE,"E89.3")])]})]}),makeQuery(id+"F29.opExtrude","SWEPT_FACE",FACE,{"disambiguationData":[OSD([sQuery(id+"F28.wireOp",EDGE,"E92.3")])]})]}),makeQuery(id+"F31.opExtrude","SWEPT_FACE",FACE,{"disambiguationData":[OSD([sQuery(id+"F30.wireOp",EDGE,"E95.1")])]})]}),makeQuery(id+"F33.opExtrude","SWEPT_FACE",FACE,{"disambiguationData":[OSD([sQuery(id+"F32.wireOp",EDGE,"E98.0")])]})]});}
            var sketch = newSketch(context, id + "F36", { "sketchPlane" : qUnion([Q0])});
            skCircle(sketch, "E108", {"center": v(-17.43, -15.33) * mm, "radius": 1.95 * mm});
            skCircle(sketch, "E109", {"center": v(-8.15, 4.87) * mm, "radius": 1.13 * mm});
            skCircle(sketch, "E110", {"center": v(-5.05, 6.25) * mm, "radius": 1.26 * mm});
            skCircle(sketch, "E111", {"center": v(19, 6.56) * mm, "radius": 1.24 * mm});
            skCircle(sketch, "E112", {"center": v(15.35, 4.52) * mm, "radius": 1.48 * mm});
            skCircle(sketch, "E113", {"center": v(19.4, 2.98) * mm, "radius": 1.34 * mm});
            skCircle(sketch, "E114", {"center": v(19.84, -35.12) * mm, "radius": 0.88 * mm});
            skCircle(sketch, "E115", {"center": v(17.38, -36.47) * mm, "radius": 0.87 * mm});
            skCircle(sketch, "E116", {"center": v(-7.2, -37.38) * mm, "radius": 1.03 * mm});
            skCircle(sketch, "E117", {"center": v(-6.67, -34.69) * mm, "radius": 0.7 * mm});
            skCircle(sketch, "E118", {"center": v(-4.31, -35.73) * mm, "radius": 1.01 * mm});
            skLineSegment(sketch, "E119.bottom", {"start": v(-14.25, -14.57) * mm, "end": v(-10.8, -14.57) * mm});
            skLineSegment(sketch, "E119.top", {"start": v(-14.25, -15.3) * mm, "end": v(-10.8, -15.3) * mm});
            skLineSegment(sketch, "E119.left", {"start": v(-14.25, -14.57) * mm, "end": v(-14.25, -15.3) * mm});
            skLineSegment(sketch, "E119.right", {"start": v(-10.8, -14.57) * mm, "end": v(-10.8, -15.3) * mm});
            skLineSegment(sketch, "E120.bottom", {"start": v(14.81, 1.38) * mm, "end": v(17.98, 1.38) * mm});
            skLineSegment(sketch, "E120.top", {"start": v(14.81, 0) * mm, "end": v(17.98, 0) * mm});
            skLineSegment(sketch, "E120.left", {"start": v(14.81, 1.38) * mm, "end": v(14.81, 0) * mm});
            skLineSegment(sketch, "E120.right", {"start": v(17.98, 1.38) * mm, "end": v(17.98, 0) * mm});
            skLineSegment(sketch, "E121.bottom", {"start": v(15.53, -31.8) * mm, "end": v(18.6, -31.8) * mm});
            skLineSegment(sketch, "E121.top", {"start": v(15.53, -33.13) * mm, "end": v(18.6, -33.13) * mm});
            skLineSegment(sketch, "E121.left", {"start": v(15.53, -31.8) * mm, "end": v(15.53, -33.13) * mm});
            skLineSegment(sketch, "E121.right", {"start": v(18.6, -31.8) * mm, "end": v(18.6, -33.13) * mm});
            skSolve(sketch);
        }
        {
            var Q0;
            Q0 = qSketchRegion(id + "F36", true);
            extrude(context, id + "F37", {"entities" : qUnion([Q0]), "operationType" : NewBodyOperationType.ADD, "depth" : 0.5 * mm, "offsetDistance" : 25.4 * mm});
        }
    });
